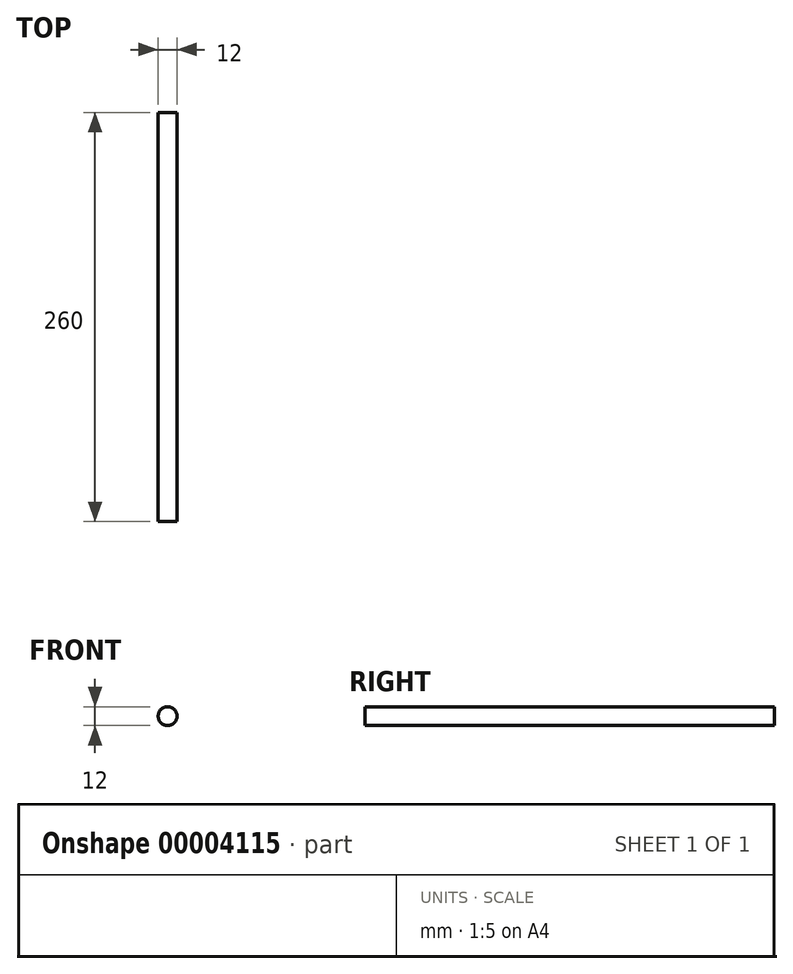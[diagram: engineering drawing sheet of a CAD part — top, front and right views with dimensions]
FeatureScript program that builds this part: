
annotation { "Feature Type Name" : "Feature", "Feature Type Description" : "" }
export const myFeature = defineFeature(function(context is Context, id is Id, definition is map)
    precondition{}
    {
        {
            var Q0;
            Q0=qCreatedBy(makeId("Front.planeOp"),FACE);
            var sketch = newSketch(context, id + "F0", { "sketchPlane" : qUnion([Q0])});
            skCircle(sketch, "E0", {"center": v(0, 0) * mm, "radius": 6 * mm});
            skSolve(sketch);
        }
        {
            var Q0;
            Q0=makeQuery(id+"F0.imprint","IMPRINT",FACE,{"disambiguationData":[TD([[makeQuery(id+"F0.imprint","IMPRINT",EDGE,{"derivedFrom":sQuery(id+"F0.wireOp",EDGE,"E0")}),1.0]])]});
            extrude(context, id + "F1", {"entities" : qUnion([Q0]), "depth" : 260 * mm});
        }
    });
